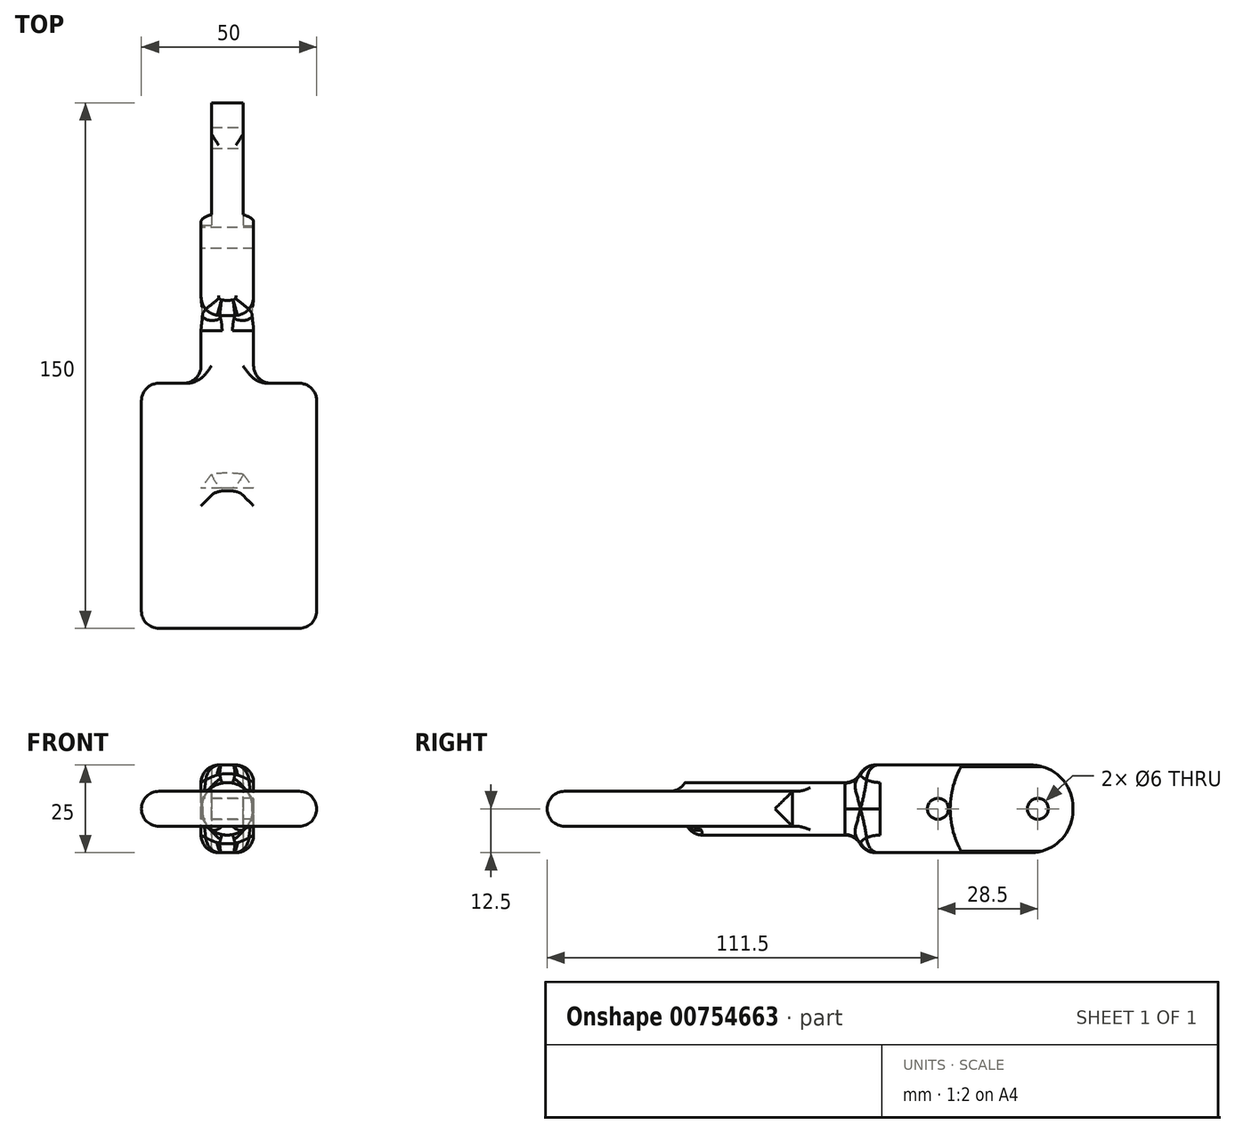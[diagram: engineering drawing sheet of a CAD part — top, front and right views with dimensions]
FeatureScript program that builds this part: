
annotation { "Feature Type Name" : "Feature", "Feature Type Description" : "" }
export const myFeature = defineFeature(function(context is Context, id is Id, definition is map)
    precondition{}
    {
        {
            var Q0;
            Q0=qCreatedBy(makeId("Right.planeOp"),FACE);
            var sketch = newSketch(context, id + "F0", { "sketchPlane" : qUnion([Q0])});
            skLineSegment(sketch, "E0.bottom", {"start": v(-10, 12.5) * mm, "end": v(50, 12.5) * mm});
            skLineSegment(sketch, "E0.top", {"start": v(-10, -12.5) * mm, "end": v(50, -12.5) * mm});
            skLineSegment(sketch, "E0.left", {"start": v(-10, 12.5) * mm, "end": v(-10, -12.5) * mm});
            skLineSegment(sketch, "E0.right", {"start": v(50, 12.5) * mm, "end": v(50, -12.5) * mm});
            skSolve(sketch);
        }
        {
            var Q0;
            Q0=makeQuery(id+"F0.imprint","IMPRINT",FACE,{"disambiguationData":[TD([[makeQuery(id+"F0.imprint","IMPRINT",EDGE,{"derivedFrom":sQuery(id+"F0.wireOp",EDGE,"E0.bottom")}),-1.0]])]});
            extrude(context, id + "F1", {"entities" : qUnion([Q0]), "depth" : 15 * mm, "offsetDistance" : 25 * mm});
        }
        {
            var Q0;
            Q0=makeQuery(id+"F1.opExtrude","SWEPT_EDGE",EDGE,{"disambiguationData":[OSD([sQuery(id+"F0.wireOp",EDGE,"E0.bottom"),sQuery(id+"F0.wireOp",EDGE,"E0.right")])]});
            var Q1;
            Q1=makeQuery(id+"F1.opExtrude","SWEPT_EDGE",EDGE,{"disambiguationData":[OSD([sQuery(id+"F0.wireOp",EDGE,"E0.top"),sQuery(id+"F0.wireOp",EDGE,"E0.right")])]});
            fillet(context, id + "F2", {"entities" : qUnion([Q0, Q1]), "radius" : 12 * mm, "tangentPropagation" : true, "allowEdgeOverflow" : false});
        }
        {
            var Q0;
            Q0=makeQuery(id+"F1.opExtrude","CAP_FACE",FACE,{"disambiguationData":[OSD([sQuery(id+"F0.wireOp",EDGE,"E0.bottom"),sQuery(id+"F0.wireOp",EDGE,"E0.top"),sQuery(id+"F0.wireOp",EDGE,"E0.left"),sQuery(id+"F0.wireOp",EDGE,"E0.right")])],"isStart":false});
            var sketch = newSketch(context, id + "F3", { "sketchPlane" : qUnion([Q0])});
            skCircle(sketch, "E1", {"center": v(40, 0) * mm, "radius": 3 * mm});
            skSolve(sketch);
        }
        {
            var Q0;
            Q0=makeQuery(id+"F3.imprint","IMPRINT",FACE,{"disambiguationData":[TD([[makeQuery(id+"F3.imprint","IMPRINT",EDGE,{"derivedFrom":sQuery(id+"F3.wireOp",EDGE,"E1")}),1.0]])]});
            extrude(context, id + "F4", {"entities" : qUnion([Q0]), "operationType" : NewBodyOperationType.REMOVE, "oppositeDirection" : true, "depth" : 25 * mm, "offsetDistance" : 25 * mm});
        }
        {
            var Q0;
            Q0=makeQuery(id+"F1.opExtrude","SWEPT_FACE",FACE,{"disambiguationData":[OSD([sQuery(id+"F0.wireOp",EDGE,"E0.left")])]});
            var sketch = newSketch(context, id + "F5", { "sketchPlane" : qUnion([Q0])});
            skCircle(sketch, "E2", {"center": v(7.5, 0) * mm, "radius": 7.5 * mm});
            skPoint(sketch, "E2.centerSnap0", {"position": v(7.5, 12.5) * mm});
            skSolve(sketch);
        }
        {
            var Q0;
            Q0 = qSketchRegion(id + "F5", true);
            extrude(context, id + "F6", {"entities" : qUnion([Q0]), "operationType" : NewBodyOperationType.ADD, "depth" : 50 * mm, "offsetDistance" : 25 * mm});
        }
        {
            var Q0;
            Q0=makeQuery(id+"F6.boolean.opBoolean","SPLIT",EDGE,{"disambiguationData":[OD(0.0)],"derivedFrom":makeQuery(id+"F6.opExtrude","CAP_EDGE",EDGE,{"disambiguationData":[OSD([sQuery(id+"F5.wireOp",EDGE,"E2")])],"isStart":true})});
            var Q1;
            Q1=makeQuery(id+"F6.boolean.opBoolean","SPLIT",EDGE,{"disambiguationData":[OD(1.0)],"derivedFrom":makeQuery(id+"F6.opExtrude","CAP_EDGE",EDGE,{"disambiguationData":[OSD([sQuery(id+"F5.wireOp",EDGE,"E2")])],"isStart":true})});
            var Q2;
            {var subQ0=sQuery(id+"F0.wireOp",EDGE,"E0.left");var subQ1=sQuery(id+"F0.wireOp",EDGE,"E0.top");Q2=makeQuery(id+"F6.boolean.opBoolean","SPLIT",EDGE,{"disambiguationData":[TD([makeQuery(id+"F1.opExtrude","SWEPT_FACE",FACE,{"disambiguationData":[OSD([subQ1])]})])],"derivedFrom":makeQuery(id+"F1.opExtrude","CAP_EDGE",EDGE,{"disambiguationData":[OSD([subQ0])],"isStart":false})});}
            var Q3;
            {var subQ0=sQuery(id+"F0.wireOp",EDGE,"E0.bottom");var subQ1=sQuery(id+"F0.wireOp",EDGE,"E0.left");Q3=makeQuery(id+"F6.boolean.opBoolean","SPLIT",EDGE,{"disambiguationData":[TD([makeQuery(id+"F1.opExtrude","SWEPT_FACE",FACE,{"disambiguationData":[OSD([subQ0])]})])],"derivedFrom":makeQuery(id+"F1.opExtrude","CAP_EDGE",EDGE,{"disambiguationData":[OSD([subQ1])],"isStart":false})});}
            var Q4;
            {var subQ0=sQuery(id+"F0.wireOp",EDGE,"E0.bottom");var subQ1=sQuery(id+"F0.wireOp",EDGE,"E0.left");Q4=makeQuery(id+"F6.boolean.opBoolean","SPLIT",EDGE,{"disambiguationData":[TD([makeQuery(id+"F1.opExtrude","SWEPT_FACE",FACE,{"disambiguationData":[OSD([subQ0])]})])],"derivedFrom":makeQuery(id+"F1.opExtrude","CAP_EDGE",EDGE,{"disambiguationData":[OSD([subQ1])],"isStart":true})});}
            var Q5;
            {var subQ0=sQuery(id+"F0.wireOp",EDGE,"E0.left");var subQ1=sQuery(id+"F0.wireOp",EDGE,"E0.top");Q5=makeQuery(id+"F6.boolean.opBoolean","SPLIT",EDGE,{"disambiguationData":[TD([makeQuery(id+"F1.opExtrude","SWEPT_FACE",FACE,{"disambiguationData":[OSD([subQ1])]})])],"derivedFrom":makeQuery(id+"F1.opExtrude","CAP_EDGE",EDGE,{"disambiguationData":[OSD([subQ0])],"isStart":true})});}
            fillet(context, id + "F7", {"entities" : qUnion([Q0, Q1, Q2, Q3, Q4, Q5]), "radius" : 5 * mm, "tangentPropagation" : true, "allowEdgeOverflow" : false});
        }
        {
            var Q0;
            Q0=makeQuery(id+"F1.opExtrude","CAP_FACE",FACE,{"disambiguationData":[OSD([sQuery(id+"F0.wireOp",EDGE,"E0.bottom"),sQuery(id+"F0.wireOp",EDGE,"E0.top"),sQuery(id+"F0.wireOp",EDGE,"E0.left"),sQuery(id+"F0.wireOp",EDGE,"E0.right")])],"isStart":false});
            var sketch = newSketch(context, id + "F8", { "sketchPlane" : qUnion([Q0])});
            skCircle(sketch, "E3", {"center": v(40, 0) * mm, "radius": 25 * mm});
            skSolve(sketch);
        }
        {
            var Q0;
            {var subQ0=sQuery(id+"F0.wireOp",EDGE,"E0.right");Q0=makeQuery(id+"F8.imprint","IMPRINT",FACE,{"disambiguationData":[TD([[makeQuery(id+"F8.imprint","IMPRINT",EDGE,{"derivedFrom":makeQuery(id+"F1.opExtrude","CAP_EDGE",EDGE,{"disambiguationData":[OSD([subQ0])],"isStart":false})}),1.0]])]});}
            var Q1;
            {var subQ0=sQuery(id+"F0.wireOp",EDGE,"E0.right");Q1=makeQuery(id+"F8.imprint","IMPRINT",FACE,{"disambiguationData":[TD([[makeQuery(id+"F8.imprint","IMPRINT",EDGE,{"derivedFrom":makeQuery(id+"F1.opExtrude","CAP_EDGE",EDGE,{"disambiguationData":[OSD([subQ0])],"isStart":false})}),-1.0]])]});}
            extrude(context, id + "F9", {"entities" : qUnion([Q0, Q1]), "operationType" : NewBodyOperationType.REMOVE, "oppositeDirection" : true, "depth" : 3 * mm, "offsetDistance" : 25 * mm});
        }
        {
            var Q0;
            Q0=makeQuery(id+"F1.opExtrude","CAP_FACE",FACE,{"disambiguationData":[OSD([sQuery(id+"F0.wireOp",EDGE,"E0.bottom"),sQuery(id+"F0.wireOp",EDGE,"E0.top"),sQuery(id+"F0.wireOp",EDGE,"E0.left"),sQuery(id+"F0.wireOp",EDGE,"E0.right")])],"isStart":true});
            var sketch = newSketch(context, id + "F10", { "sketchPlane" : qUnion([Q0])});
            skCircle(sketch, "E4", {"center": v(-40, 0) * mm, "radius": 25 * mm});
            skSolve(sketch);
        }
        {
            var Q0;
            Q0 = qSketchRegion(id + "F10", true);
            extrude(context, id + "F11", {"entities" : qUnion([Q0]), "operationType" : NewBodyOperationType.REMOVE, "oppositeDirection" : true, "depth" : 3 * mm, "offsetDistance" : 25 * mm});
        }
        {
            var Q0;
            Q0=makeQuery(id+"F1.opExtrude","CAP_FACE",FACE,{"disambiguationData":[OSD([sQuery(id+"F0.wireOp",EDGE,"E0.bottom"),sQuery(id+"F0.wireOp",EDGE,"E0.top"),sQuery(id+"F0.wireOp",EDGE,"E0.left"),sQuery(id+"F0.wireOp",EDGE,"E0.right")])],"isStart":true});
            var sketch = newSketch(context, id + "F12", { "sketchPlane" : qUnion([Q0])});
            skCircle(sketch, "E5", {"center": v(-11.5, 0) * mm, "radius": 3 * mm});
            skSolve(sketch);
        }
        {
            var Q0;
            Q0=makeQuery(id+"F12.imprint","IMPRINT",FACE,{"disambiguationData":[TD([[makeQuery(id+"F12.imprint","IMPRINT",EDGE,{"derivedFrom":sQuery(id+"F12.wireOp",EDGE,"E5")}),1.0]])]});
            extrude(context, id + "F13", {"entities" : qUnion([Q0]), "operationType" : NewBodyOperationType.REMOVE, "endBound" : BoundingType.THROUGH_ALL, "oppositeDirection" : true, "depth" : 25 * mm, "offsetDistance" : 25 * mm});
        }
        {
            var Q0;
            Q0=qCreatedBy(makeId("Top.planeOp"),FACE);
            var sketch = newSketch(context, id + "F14", { "sketchPlane" : qUnion([Q0])});
            skLineSegment(sketch, "E6.bottom", {"start": v(-17, -30) * mm, "end": v(33, -30) * mm});
            skLineSegment(sketch, "E6.top", {"start": v(-17, -100) * mm, "end": v(33, -100) * mm});
            skLineSegment(sketch, "E6.left", {"start": v(-17, -30) * mm, "end": v(-17, -100) * mm});
            skLineSegment(sketch, "E6.right", {"start": v(33, -30) * mm, "end": v(33, -100) * mm});
            skSolve(sketch);
        }
        {
            var Q0;
            Q0=makeQuery(id+"F14.imprint","IMPRINT",FACE,{"disambiguationData":[TD([[makeQuery(id+"F14.imprint","IMPRINT",EDGE,{"derivedFrom":sQuery(id+"F14.wireOp",EDGE,"E6.bottom")}),-1.0]])]});
            extrude(context, id + "F15", {"entities" : qUnion([Q0]), "operationType" : NewBodyOperationType.ADD, "endBound" : BoundingType.SYMMETRIC, "depth" : 10 * mm, "offsetDistance" : 25 * mm});
        }
        {
            var Q0;
            Q0=makeQuery(id+"F15.opExtrude","SWEPT_EDGE",EDGE,{"disambiguationData":[OSD([sQuery(id+"F14.wireOp",EDGE,"E6.top"),sQuery(id+"F14.wireOp",EDGE,"E6.left")])]});
            var Q1;
            Q1=makeQuery(id+"F15.opExtrude","SWEPT_FACE",FACE,{"disambiguationData":[OSD([sQuery(id+"F14.wireOp",EDGE,"E6.left")])]});
            var Q2;
            Q2=makeQuery(id+"F15.opExtrude","SWEPT_FACE",FACE,{"disambiguationData":[OSD([sQuery(id+"F14.wireOp",EDGE,"E6.right")])]});
            var Q3;
            Q3=makeQuery(id+"F15.opExtrude","SWEPT_FACE",FACE,{"disambiguationData":[OSD([sQuery(id+"F14.wireOp",EDGE,"E6.top")])]});
            fillet(context, id + "F16", {"entities" : qUnion([Q0, Q1, Q2, Q3]), "radius" : 5 * mm, "tangentPropagation" : true, "allowEdgeOverflow" : false});
        }
        {
            var Q0;
            Q0=makeQuery(id+"F15.boolean.opBoolean","INTERSECT",EDGE,{"derivedFrom":[makeQuery(id+"F6.opExtrude","CAP_FACE",FACE,{"disambiguationData":[OSD([sQuery(id+"F5.wireOp",EDGE,"E2")])],"isStart":false}),makeQuery(id+"F15.opExtrude","CAP_FACE",FACE,{"disambiguationData":[OSD([sQuery(id+"F14.wireOp",EDGE,"E6.bottom"),sQuery(id+"F14.wireOp",EDGE,"E6.top"),sQuery(id+"F14.wireOp",EDGE,"E6.left"),sQuery(id+"F14.wireOp",EDGE,"E6.right")])],"isStart":false})]});
            var Q1;
            Q1=makeQuery(id+"F15.boolean.opBoolean","INTERSECT",EDGE,{"disambiguationData":[OD(0.0)],"derivedFrom":[makeQuery(id+"F6.opExtrude","SWEPT_FACE",FACE,{"disambiguationData":[OSD([sQuery(id+"F5.wireOp",EDGE,"E2")])]}),makeQuery(id+"F15.opExtrude","SWEPT_FACE",FACE,{"disambiguationData":[OSD([sQuery(id+"F14.wireOp",EDGE,"E6.bottom")])]})]});
            var Q2;
            Q2=makeQuery(id+"F15.boolean.opBoolean","INTERSECT",EDGE,{"disambiguationData":[OD(1.0)],"derivedFrom":[makeQuery(id+"F6.opExtrude","SWEPT_FACE",FACE,{"disambiguationData":[OSD([sQuery(id+"F5.wireOp",EDGE,"E2")])]}),makeQuery(id+"F15.opExtrude","SWEPT_FACE",FACE,{"disambiguationData":[OSD([sQuery(id+"F14.wireOp",EDGE,"E6.bottom")])]})]});
            fillet(context, id + "F17", {"entities" : qUnion([Q0, Q1, Q2]), "radius" : 5 * mm, "tangentPropagation" : true, "allowEdgeOverflow" : false});
        }
        {
            var Q0;
            Q0=makeQuery(id+"F15.boolean.opBoolean","INTERSECT",EDGE,{"disambiguationData":[OD(0.0)],"derivedFrom":[makeQuery(id+"F6.opExtrude","SWEPT_FACE",FACE,{"disambiguationData":[OSD([sQuery(id+"F5.wireOp",EDGE,"E2")])]}),makeQuery(id+"F15.opExtrude","CAP_FACE",FACE,{"disambiguationData":[OSD([sQuery(id+"F14.wireOp",EDGE,"E6.bottom"),sQuery(id+"F14.wireOp",EDGE,"E6.top"),sQuery(id+"F14.wireOp",EDGE,"E6.left"),sQuery(id+"F14.wireOp",EDGE,"E6.right")])],"isStart":false})]});
            var Q1;
            Q1=makeQuery(id+"F15.boolean.opBoolean","INTERSECT",EDGE,{"disambiguationData":[OD(1.0)],"derivedFrom":[makeQuery(id+"F6.opExtrude","SWEPT_FACE",FACE,{"disambiguationData":[OSD([sQuery(id+"F5.wireOp",EDGE,"E2")])]}),makeQuery(id+"F15.opExtrude","CAP_FACE",FACE,{"disambiguationData":[OSD([sQuery(id+"F14.wireOp",EDGE,"E6.bottom"),sQuery(id+"F14.wireOp",EDGE,"E6.top"),sQuery(id+"F14.wireOp",EDGE,"E6.left"),sQuery(id+"F14.wireOp",EDGE,"E6.right")])],"isStart":false})]});
            var Q2;
            Q2=makeQuery(id+"F15.boolean.opBoolean","INTERSECT",EDGE,{"disambiguationData":[OD(0.0)],"derivedFrom":[makeQuery(id+"F6.opExtrude","SWEPT_FACE",FACE,{"disambiguationData":[OSD([sQuery(id+"F5.wireOp",EDGE,"E2")])]}),makeQuery(id+"F15.opExtrude","CAP_FACE",FACE,{"disambiguationData":[OSD([sQuery(id+"F14.wireOp",EDGE,"E6.bottom"),sQuery(id+"F14.wireOp",EDGE,"E6.top"),sQuery(id+"F14.wireOp",EDGE,"E6.left"),sQuery(id+"F14.wireOp",EDGE,"E6.right")])],"isStart":true})]});
            var Q3;
            Q3=makeQuery(id+"F15.boolean.opBoolean","INTERSECT",EDGE,{"disambiguationData":[OD(1.0)],"derivedFrom":[makeQuery(id+"F6.opExtrude","SWEPT_FACE",FACE,{"disambiguationData":[OSD([sQuery(id+"F5.wireOp",EDGE,"E2")])]}),makeQuery(id+"F15.opExtrude","CAP_FACE",FACE,{"disambiguationData":[OSD([sQuery(id+"F14.wireOp",EDGE,"E6.bottom"),sQuery(id+"F14.wireOp",EDGE,"E6.top"),sQuery(id+"F14.wireOp",EDGE,"E6.left"),sQuery(id+"F14.wireOp",EDGE,"E6.right")])],"isStart":true})]});
            fillet(context, id + "F18", {"entities" : qUnion([Q0, Q1, Q2, Q3]), "radius" : 5 * mm, "tangentPropagation" : true, "allowEdgeOverflow" : false});
        }
        {
            var Q0;
            {var subQ0=sQuery(id+"F5.wireOp",EDGE,"E2");Q0=makeQuery(id+"F15.boolean.opBoolean","SPLIT",EDGE,{"disambiguationData":[TD([makeQuery(id+"F15.opExtrude","CAP_FACE",FACE,{"disambiguationData":[OSD([sQuery(id+"F14.wireOp",EDGE,"E6.bottom"),sQuery(id+"F14.wireOp",EDGE,"E6.top"),sQuery(id+"F14.wireOp",EDGE,"E6.left"),sQuery(id+"F14.wireOp",EDGE,"E6.right")])],"isStart":true})])],"derivedFrom":makeQuery(id+"F6.opExtrude","CAP_EDGE",EDGE,{"disambiguationData":[OSD([subQ0])],"isStart":false})});}
            fillet(context, id + "F19", {"entities" : qUnion([Q0]), "radius" : 5 * mm, "tangentPropagation" : true, "allowEdgeOverflow" : false});
        }
        {
            var Q0;
            Q0=makeQuery(id+"F1.opExtrude","SWEPT_EDGE",EDGE,{"disambiguationData":[OSD([sQuery(id+"F0.wireOp",EDGE,"E0.bottom"),sQuery(id+"F0.wireOp",EDGE,"E0.left")])]});
            var Q1;
            {var subQ0=sQuery(id+"F0.wireOp",EDGE,"E0.left");var subQ1=makeQuery(id+"F1.opExtrude","SWEPT_FACE",FACE,{"disambiguationData":[OSD([subQ0])]});var subQ2=sQuery(id+"F0.wireOp",EDGE,"E0.top");var subQ3=sQuery(id+"F5.wireOp",EDGE,"E2");Q1=makeQuery(id+"F7.opFillet","BLEND_EDGE",EDGE,{"disambiguationData":[OD(1.0)],"blendedFrom":[makeQuery(id+"F6.boolean.opBoolean","SPLIT",EDGE,{"disambiguationData":[OD(1.0)],"derivedFrom":makeQuery(id+"F6.opExtrude","CAP_EDGE",EDGE,{"disambiguationData":[OSD([subQ3])],"isStart":true})}),makeQuery(id+"F6.boolean.opBoolean","SPLIT",FACE,{"disambiguationData":[TD([makeQuery(id+"F1.opExtrude","SWEPT_FACE",FACE,{"disambiguationData":[OSD([subQ2])]})])],"derivedFrom":subQ1})],"blendedInto":[makeQuery(id+"F6.boolean.opBoolean","SPLIT",FACE,{"disambiguationData":[TD([makeQuery(id+"F1.opExtrude","SWEPT_FACE",FACE,{"disambiguationData":[OSD([subQ2])]})])],"derivedFrom":subQ1})]});}
            var Q2;
            Q2=makeQuery(id+"F1.opExtrude","SWEPT_EDGE",EDGE,{"disambiguationData":[OSD([sQuery(id+"F0.wireOp",EDGE,"E0.top"),sQuery(id+"F0.wireOp",EDGE,"E0.left")])]});
            fillet(context, id + "F20", {"entities" : qUnion([Q0, Q1, Q2]), "radius" : 5 * mm, "tangentPropagation" : true, "allowEdgeOverflow" : false});
        }
    });
